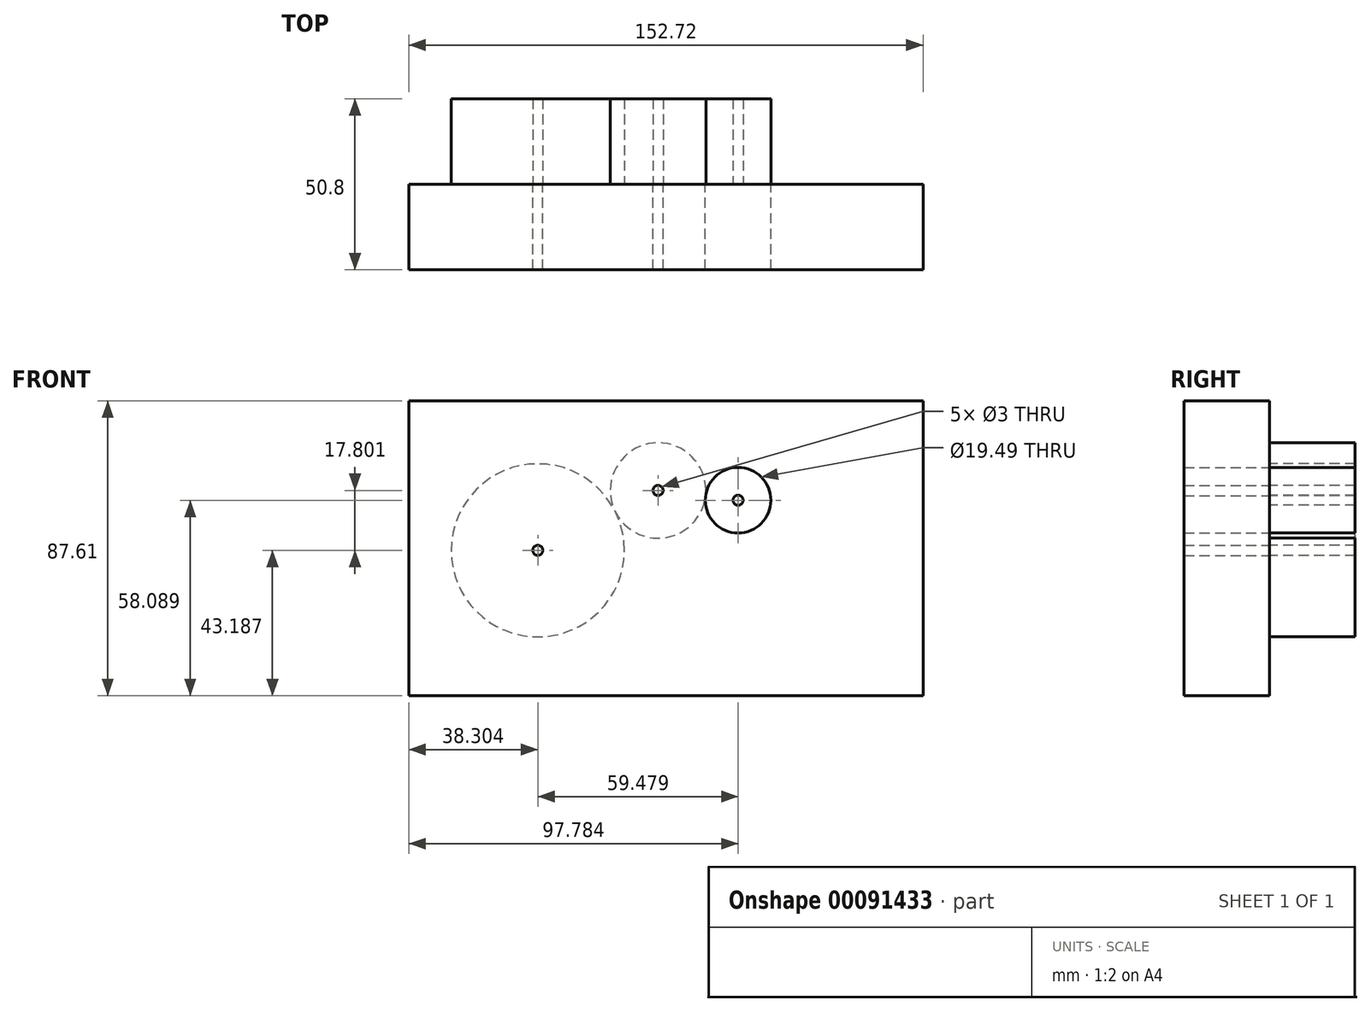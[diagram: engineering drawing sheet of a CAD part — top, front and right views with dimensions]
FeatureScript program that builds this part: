
annotation { "Feature Type Name" : "Feature", "Feature Type Description" : "" }
export const myFeature = defineFeature(function(context is Context, id is Id, definition is map)
    precondition{}
    {
        {
            var Q0;
            Q0=qCreatedBy(makeId("Front.planeOp"),FACE);
            var sketch = newSketch(context, id + "F0", { "sketchPlane" : qUnion([Q0])});
            skLineSegment(sketch, "E0.bottom", {"start": v(76.75, -55.94) * mm, "end": v(-75.97, -55.94) * mm});
            skLineSegment(sketch, "E0.top", {"start": v(76.75, 31.67) * mm, "end": v(-75.97, 31.67) * mm});
            skLineSegment(sketch, "E0.left", {"start": v(76.75, -55.94) * mm, "end": v(76.75, 31.67) * mm});
            skLineSegment(sketch, "E0.right", {"start": v(-75.97, -55.94) * mm, "end": v(-75.97, 31.67) * mm});
            skCircle(sketch, "E1", {"center": v(-37.67, -12.75) * mm, "radius": 25.72 * mm});
            skCircle(sketch, "E2", {"center": v(-1.95, 5.05) * mm, "radius": 14.2 * mm});
            skCircle(sketch, "E3", {"center": v(21.81, 2.15) * mm, "radius": 9.75 * mm});
            skSolve(sketch);
        }
        {
            var Q0;
            Q0=makeQuery(id+"F0.imprint","IMPRINT",FACE,{"disambiguationData":[TD([[makeQuery(id+"F0.imprint","IMPRINT",EDGE,{"derivedFrom":sQuery(id+"F0.wireOp",EDGE,"E0.bottom")}),-1.0]])]});
            var Q1;
            Q1=makeQuery(id+"F0.imprint","IMPRINT",FACE,{"disambiguationData":[TD([[makeQuery(id+"F0.imprint","IMPRINT",EDGE,{"derivedFrom":sQuery(id+"F0.wireOp",EDGE,"E1")}),1.0]])]});
            var Q2;
            Q2=makeQuery(id+"F0.imprint","IMPRINT",FACE,{"disambiguationData":[TD([[makeQuery(id+"F0.imprint","IMPRINT",EDGE,{"derivedFrom":sQuery(id+"F0.wireOp",EDGE,"E2")}),1.0]])]});
            extrude(context, id + "F1", {"entities" : qUnion([Q0, Q1, Q2]), "depth" : 25.4 * mm});
        }
        {
            var Q0;
            Q0=makeQuery(id+"F0.imprint","IMPRINT",FACE,{"disambiguationData":[TD([[makeQuery(id+"F0.imprint","IMPRINT",EDGE,{"derivedFrom":sQuery(id+"F0.wireOp",EDGE,"E1")}),1.0]])]});
            extrude(context, id + "F2", {"entities" : qUnion([Q0]), "oppositeDirection" : true, "depth" : 25.4 * mm});
        }
        {
            var Q0;
            Q0=makeQuery(id+"F1.opExtrude","CAP_FACE",FACE,{"disambiguationData":[OSD([sQuery(id+"F0.wireOp",EDGE,"E0.bottom"),sQuery(id+"F0.wireOp",EDGE,"E0.top"),sQuery(id+"F0.wireOp",EDGE,"E0.left"),sQuery(id+"F0.wireOp",EDGE,"E0.right")])],"isStart":true});
            var sketch = newSketch(context, id + "F3", { "sketchPlane" : qUnion([Q0])});
            skSolve(sketch);
        }
        {
            var Q0;
            Q0=makeQuery(id+"F0.imprint","IMPRINT",FACE,{"disambiguationData":[TD([[makeQuery(id+"F0.imprint","IMPRINT",EDGE,{"derivedFrom":sQuery(id+"F0.wireOp",EDGE,"E3")}),1.0]])]});
            extrude(context, id + "F4", {"entities" : qUnion([Q0]), "depth" : 25.4 * mm});
        }
        {
            var Q0;
            {var subQ0=sQuery(id+"F0.wireOp",EDGE,"E2");var subQ1=makeQuery(id+"F0.imprint","INTERSECT",VERTEX,{"derivedFrom":[sQuery(id+"F0.wireOp",EDGE,"E1"),subQ0]});Q0=makeQuery(id+"F0.imprint","IMPRINT",FACE,{"disambiguationData":[TD([[makeQuery(id+"F0.imprint","IMPRINT",EDGE,{"disambiguationData":[TD([[subQ1,-1.0]])],"derivedFrom":subQ0}),1.0]])]});}
            extrude(context, id + "F5", {"entities" : qUnion([Q0]), "oppositeDirection" : true, "depth" : 25.4 * mm});
        }
        {
            var Q0;
            Q0=makeQuery(id+"F3.imprint","IMPRINT",FACE,{"disambiguationData":[TD([[makeQuery(id+"F3.imprint","IMPRINT",EDGE,{"derivedFrom":makeQuery(id+"F1.opExtrude","CAP_EDGE",EDGE,{"disambiguationData":[OSD([sQuery(id+"F0.wireOp",EDGE,"E3")])],"isStart":true})}),-1.0]])]});
            extrude(context, id + "F6", {"entities" : qUnion([Q0]), "depth" : 25.4 * mm});
        }
        {
            var Q0;
            Q0=makeQuery(id+"F4.opExtrude","SWEPT_BODY",BODY,{"disambiguationData":[OSD([sQuery(id+"F0.wireOp",EDGE,"E3"),sQuery(id+"F0.wireOp",EDGE,"HMtkWY2F-2zKA-zkzh-vpno-3N1tvToLgrLy")])]});
            deleteBodies(context, id + "F7", {"entities" : qUnion([Q0])});
        }
        {
            var Q0;
            Q0=sQuery(id+"F0.wireOp",VERTEX,"E3.center");
            var Q1;
            Q1=makeQuery(id+"F6.opExtrude","SWEPT_BODY",BODY,{"disambiguationData":[OSD([sQuery(id+"F0.wireOp",EDGE,"E3")])]});
            hole(context, id + "F8", {"style" : HoleStyle.SIMPLE, "endStyle" : HoleEndStyle.THROUGH, "holeDiameter" : 3 * mm, "locations" : qUnion([Q0]), "scope" : qUnion([Q1]), "isTappedThrough" : true});
        }
        {
            var Q0;
            Q0=sQuery(id+"F0.wireOp",VERTEX,"E2.center");
            var Q1;
            Q1=makeQuery(id+"F5.opExtrude","SWEPT_BODY",BODY,{"disambiguationData":[OSD([sQuery(id+"F0.wireOp",EDGE,"E2")])]});
            hole(context, id + "F9", {"style" : HoleStyle.SIMPLE, "endStyle" : HoleEndStyle.THROUGH, "holeDiameter" : 3 * mm, "locations" : qUnion([Q0]), "scope" : qUnion([Q1]), "isTappedThrough" : true});
        }
        {
            var Q0;
            Q0=sQuery(id+"F0.wireOp",VERTEX,"E1.center");
            var Q1;
            Q1=makeQuery(id+"F2.opExtrude","SWEPT_BODY",BODY,{"disambiguationData":[OSD([sQuery(id+"F0.wireOp",EDGE,"E1")])]});
            hole(context, id + "F10", {"style" : HoleStyle.SIMPLE, "endStyle" : HoleEndStyle.THROUGH, "holeDiameter" : 3 * mm, "locations" : qUnion([Q0]), "scope" : qUnion([Q1]), "isTappedThrough" : true});
        }
        {
            var Q0;
            Q0=sQuery(id+"F0.wireOp",VERTEX,"E2.center");
            var Q1;
            Q1=makeQuery(id+"F1.opExtrude","SWEPT_BODY",BODY,{"disambiguationData":[OSD([sQuery(id+"F0.wireOp",EDGE,"E0.bottom"),sQuery(id+"F0.wireOp",EDGE,"E0.top"),sQuery(id+"F0.wireOp",EDGE,"E0.left"),sQuery(id+"F0.wireOp",EDGE,"E0.right"),sQuery(id+"F0.wireOp",EDGE,"E3")])]});
            hole(context, id + "F11", {"style" : HoleStyle.SIMPLE, "endStyle" : HoleEndStyle.THROUGH, "oppositeDirection" : true, "holeDiameter" : 3 * mm, "locations" : qUnion([Q0]), "scope" : qUnion([Q1]), "isTappedThrough" : true});
        }
        {
            var Q0;
            Q0=sQuery(id+"F0.wireOp",VERTEX,"E1.center");
            var Q1;
            Q1=makeQuery(id+"F1.opExtrude","SWEPT_BODY",BODY,{"disambiguationData":[OSD([sQuery(id+"F0.wireOp",EDGE,"E0.bottom"),sQuery(id+"F0.wireOp",EDGE,"E0.top"),sQuery(id+"F0.wireOp",EDGE,"E0.left"),sQuery(id+"F0.wireOp",EDGE,"E0.right"),sQuery(id+"F0.wireOp",EDGE,"E3")])]});
            hole(context, id + "F12", {"style" : HoleStyle.SIMPLE, "endStyle" : HoleEndStyle.THROUGH, "oppositeDirection" : true, "holeDiameter" : 3 * mm, "locations" : qUnion([Q0]), "scope" : qUnion([Q1]), "isTappedThrough" : true});
        }
    });
